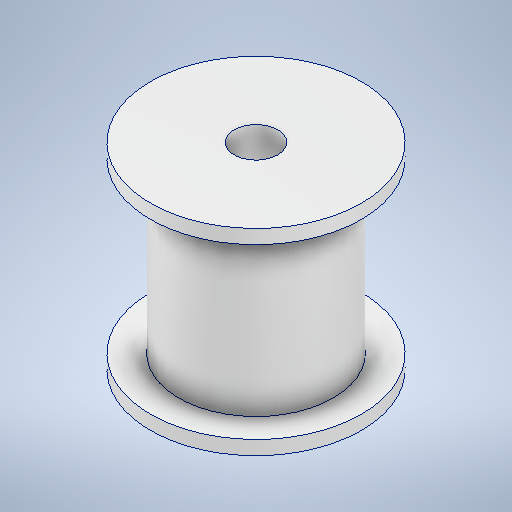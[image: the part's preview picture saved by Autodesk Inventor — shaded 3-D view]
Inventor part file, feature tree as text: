
AUTODESK INVENTOR PART (.ipt)
format: ipt  version: 2025.1 (Build 291241000, 241)  size: 285,184 bytes
history: native  units: mm
features: sketch x2, other x1, hole x1
ambient origin geometry x8: Origin, YZ Plane, XZ Plane, XY Plane, X Axis, Y Axis, Z Axis, Center Point
bodies: Solide1 (feature_tree)
feature tree (4):
  other  "Révolution1"
  hole  "Perçage1"  [1 undecoded]
  sketch  "Esquisse2"
  sketch  "Esquisse3"
note: 1 required parameter value undecoded (feature->parameter linkage not recoverable at this tier; creation-order binding heuristic only, values carry confidence <= 0.55)
